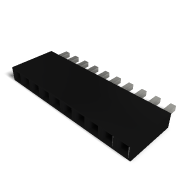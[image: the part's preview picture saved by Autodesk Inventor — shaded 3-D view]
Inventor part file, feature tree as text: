
AUTODESK INVENTOR PART (.ipt)
format: ipt  version: 2020 (Build 240168000, 168)  size: 287,232 bytes
history: native  units: in
note: dims shown in document units (in); Inventor stores cm internally (conversion verified against a paired STEP export)
features: extrude x3, sketch x3, chamfer x2, pattern_linear x1
ambient origin geometry x8: Origin, YZ Plane, XZ Plane, XY Plane, X Axis, Y Axis, Z Axis, Center Point
bodies: Solid1 (feature_tree)
feature tree (9):
  extrude  "Extrusion1"  Depth=0.1in
  extrude  "Extrusion2"  Depth=0.045in
  chamfer  "Chamfer1"  Distance=0.25in
  extrude  "Extrusion3"  Depth=0.035in
  chamfer  "Chamfer2"  Distance=0.13in
  pattern_linear  "Rectangular Pattern1"  Spacing1=0.015in  [1 undecoded]
  sketch  "Sketch1"  dims[d0=0.1in d1=0.1in]
  sketch  "Sketch2"  dims[d2=0.33in d3=0.0in d4=0.045in d5=0.25in d6=0.0in]
  sketch  "Sketch3"  dims[d7=0.015in d8=0.125in d9=45.0deg d10=0.035in d11=0.13in d12=0.0in d13=0.015in d14=0.125in d15=45.0deg d16=3.937in d18=0.1in]
note: 1 required parameter value undecoded (feature->parameter linkage not recoverable at this tier; creation-order binding heuristic only, values carry confidence <= 0.55)
